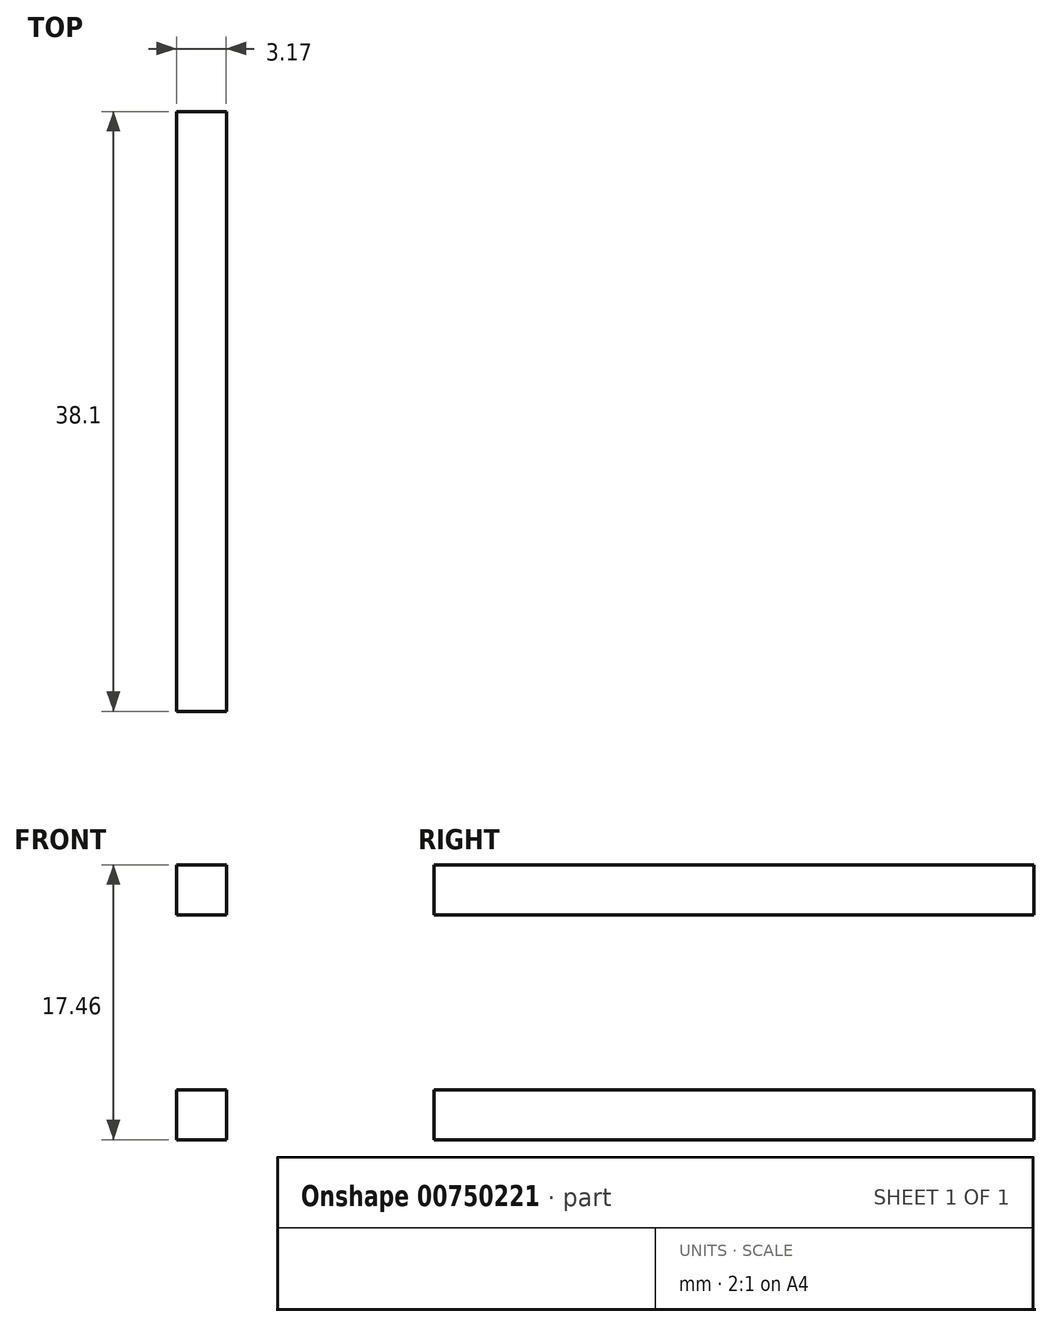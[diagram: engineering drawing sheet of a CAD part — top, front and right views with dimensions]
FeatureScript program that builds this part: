
annotation { "Feature Type Name" : "Feature", "Feature Type Description" : "" }
export const myFeature = defineFeature(function(context is Context, id is Id, definition is map)
    precondition{}
    {
        {
            var Q0;
            Q0=qCreatedBy(makeId("Right.planeOp"),FACE);
            var sketch = newSketch(context, id + "F0", { "sketchPlane" : qUnion([Q0])});
            skLineSegment(sketch, "E0.bottom", {"start": v(0, 0) * mm, "end": v(47.63, 0) * mm});
            skLineSegment(sketch, "E0.top", {"start": v(0, 17.46) * mm, "end": v(47.63, 17.46) * mm});
            skLineSegment(sketch, "E0.left", {"start": v(0, 0) * mm, "end": v(0, 17.46) * mm});
            skLineSegment(sketch, "E0.right", {"start": v(47.63, 0) * mm, "end": v(47.63, 17.46) * mm});
            skLineSegment(sketch, "E1.bottom", {"start": v(0, 17.46) * mm, "end": v(4.76, 17.46) * mm});
            skLineSegment(sketch, "E1.top", {"start": v(0, 0) * mm, "end": v(4.76, 0) * mm});
            skLineSegment(sketch, "E1.left", {"start": v(0, 17.46) * mm, "end": v(0, 0) * mm});
            skLineSegment(sketch, "E1.right", {"start": v(4.76, 17.46) * mm, "end": v(4.76, 0) * mm});
            skLineSegment(sketch, "E2.bottom", {"start": v(47.63, 17.46) * mm, "end": v(42.86, 17.46) * mm});
            skLineSegment(sketch, "E2.top", {"start": v(47.63, 0) * mm, "end": v(42.86, 0) * mm});
            skLineSegment(sketch, "E2.left", {"start": v(47.63, 17.46) * mm, "end": v(47.63, 0) * mm});
            skLineSegment(sketch, "E2.right", {"start": v(42.86, 17.46) * mm, "end": v(42.86, 0) * mm});
            skPoint(sketch, "E3.oppositeSnap0", {"position": v(2.38, 17.46) * mm});
            skLineSegment(sketch, "E3.bottom", {"start": v(0, 17.46) * mm, "end": v(2.38, 17.46) * mm});
            skLineSegment(sketch, "E3.top", {"start": v(0, 8.73) * mm, "end": v(2.38, 8.73) * mm, "construction": true});
            skLineSegment(sketch, "E3.left", {"start": v(0, 17.46) * mm, "end": v(0, 8.73) * mm});
            skLineSegment(sketch, "E3.right", {"start": v(2.38, 17.46) * mm, "end": v(2.38, 8.73) * mm, "construction": true});
            skPoint(sketch, "E4", {"position": v(4.76, 8.73) * mm});
            skCircle(sketch, "E5", {"center": v(2.38, 8.73) * mm, "radius": 0.75 * mm});
            skPoint(sketch, "E6.oppositeSnap0", {"position": v(47.63, 8.73) * mm});
            skPoint(sketch, "E6.oppositeSnap1", {"position": v(45.24, 17.46) * mm});
            skLineSegment(sketch, "E6.bottom", {"start": v(47.63, 17.46) * mm, "end": v(45.24, 17.46) * mm, "construction": true});
            skLineSegment(sketch, "E6.top", {"start": v(47.63, 8.73) * mm, "end": v(45.24, 8.73) * mm, "construction": true});
            skLineSegment(sketch, "E6.left", {"start": v(47.63, 17.46) * mm, "end": v(47.63, 8.73) * mm, "construction": true});
            skLineSegment(sketch, "E6.right", {"start": v(45.24, 17.46) * mm, "end": v(45.24, 8.73) * mm, "construction": true});
            skCircle(sketch, "E7", {"center": v(45.24, 8.73) * mm, "radius": 0.75 * mm});
            skLineSegment(sketch, "E8.bottom", {"start": v(42.86, 14.29) * mm, "end": v(4.76, 14.29) * mm});
            skLineSegment(sketch, "E8.top", {"start": v(42.86, 3.18) * mm, "end": v(4.76, 3.18) * mm});
            skLineSegment(sketch, "E8.left", {"start": v(42.86, 14.29) * mm, "end": v(42.86, 3.18) * mm});
            skLineSegment(sketch, "E8.right", {"start": v(4.76, 14.29) * mm, "end": v(4.76, 3.18) * mm});
            skPoint(sketch, "E8.middle", {"position": v(23.81, 8.73) * mm});
            skPoint(sketch, "E8.middle.positionSnap0", {"position": v(23.81, 17.46) * mm});
            skPoint(sketch, "E8.centerSnap0", {"position": v(23.81, 17.46) * mm});
            skSolve(sketch);
        }
        {
            var Q0;
            {var subQ1=sQuery(id+"F0.wireOp",EDGE,"E1.bottom");Q0=makeQuery(id+"F0.imprint","IMPRINT",FACE,{"disambiguationData":[TD([[makeQuery(id+"F0.imprint","IMPRINT",EDGE,{"derivedFrom":subQ1}),-1.0]])]});}
            var Q1;
            {var subQ0=sQuery(id+"F0.wireOp",EDGE,"E0.bottom");Q1=makeQuery(id+"F0.imprint","IMPRINT",FACE,{"disambiguationData":[TD([[makeQuery(id+"F0.imprint","IMPRINT",EDGE,{"derivedFrom":subQ0}),1.0]])]});}
            var Q2;
            {var subQ0=sQuery(id+"F0.wireOp",EDGE,"E0.top");Q2=makeQuery(id+"F0.imprint","IMPRINT",FACE,{"disambiguationData":[TD([[makeQuery(id+"F0.imprint","IMPRINT",EDGE,{"derivedFrom":subQ0}),-1.0]])]});}
            var Q3;
            {var subQ1=sQuery(id+"F0.wireOp",EDGE,"E2.bottom");Q3=makeQuery(id+"F0.imprint","IMPRINT",FACE,{"disambiguationData":[TD([[makeQuery(id+"F0.imprint","IMPRINT",EDGE,{"derivedFrom":subQ1}),1.0]])]});}
            extrude(context, id + "F1", {"entities" : qUnion([Q0, Q1, Q2, Q3]), "depth" : 3.17 * mm, "offsetDistance" : 25.4 * mm});
        }
    });
